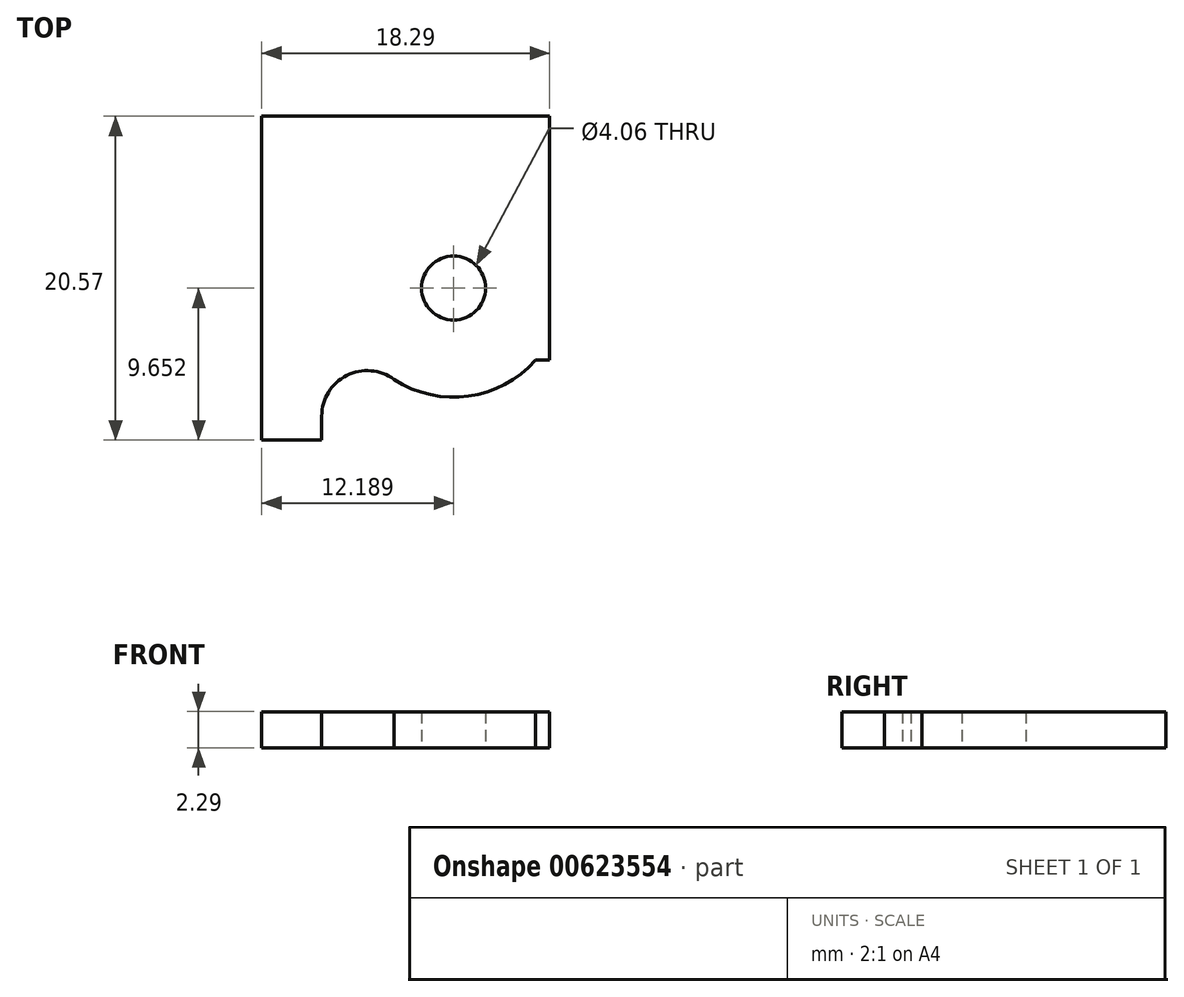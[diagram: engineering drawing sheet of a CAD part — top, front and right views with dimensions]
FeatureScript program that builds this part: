
annotation { "Feature Type Name" : "Feature", "Feature Type Description" : "" }
export const myFeature = defineFeature(function(context is Context, id is Id, definition is map)
    precondition{}
    {
        {
            var Q0;
            Q0=qCreatedBy(makeId("Top.planeOp"),FACE);
            var sketch = newSketch(context, id + "F0", { "sketchPlane" : qUnion([Q0])});
            skLineSegment(sketch, "E0", {"start": v(34.18, 2.04) * mm, "end": v(34.18, -13.45) * mm});
            skLineSegment(sketch, "E1", {"start": v(34.18, 2.04) * mm, "end": v(15.9, 2.04) * mm});
            skLineSegment(sketch, "E2", {"start": v(15.9, 2.04) * mm, "end": v(15.9, -13.45) * mm});
            skLineSegment(sketch, "E3", {"start": v(34.18, -13.45) * mm, "end": v(34.18, -8.88) * mm});
            skCircle(sketch, "E4", {"center": v(28.08, -8.88) * mm, "radius": 2.03 * mm});
            skArc(sketch, "E5", {"start": v(24.1, -14.55) * mm, "mid": v(28.9, -15.76) * mm, "end": v(33.28, -13.45) * mm});
            skLineSegment(sketch, "E6.trimOffspring", {"start": v(33.28, -13.45) * mm, "end": v(34.18, -13.45) * mm});
            skLineSegment(sketch, "E7", {"start": v(15.9, 2.04) * mm, "end": v(15.9, -18.53) * mm});
            skLineSegment(sketch, "E8", {"start": v(15.9, -18.53) * mm, "end": v(19.7, -18.53) * mm});
            skLineSegment(sketch, "E9", {"start": v(19.7, -18.53) * mm, "end": v(19.7, -17) * mm});
            skArc(sketch, "E10", {"start": v(24.3, -14.68) * mm, "mid": v(21.29, -14.43) * mm, "end": v(19.7, -17) * mm});
            skSolve(sketch);
        }
        {
            var Q0;
            Q0=makeQuery(id+"F0.imprint","IMPRINT",FACE,{"disambiguationData":[TD([[makeQuery(id+"F0.imprint","IMPRINT",EDGE,{"derivedFrom":sQuery(id+"F0.wireOp",EDGE,"E0")}),-1.0]])]});
            extrude(context, id + "F1", {"entities" : qUnion([Q0]), "depth" : 2.3 * mm, "offsetDistance" : 25.4 * mm});
        }
    });
